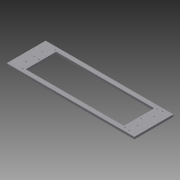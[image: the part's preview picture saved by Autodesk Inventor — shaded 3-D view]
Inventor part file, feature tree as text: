
AUTODESK INVENTOR PART (.ipt)
format: ipt  version: 2014 SP1 (Build 180222100, 222)  size: 90,624 bytes
history: native  units: in
note: dims shown in document units (in); Inventor stores cm internally (conversion verified against a paired STEP export)
features: extrude x1, sketch x1
ambient origin geometry x8: Origin, YZ Plane, XZ Plane, XY Plane, X Axis, Y Axis, Z Axis, Center Point
bodies: Solid1 (feature_tree)
feature tree (2):
  extrude  "Extrusion1"  [1 undecoded]
  sketch  "Sketch1"  dims[d0=0.1875in d1=0.0in]
note: 1 required parameter value undecoded (feature->parameter linkage not recoverable at this tier; creation-order binding heuristic only, values carry confidence <= 0.55)
